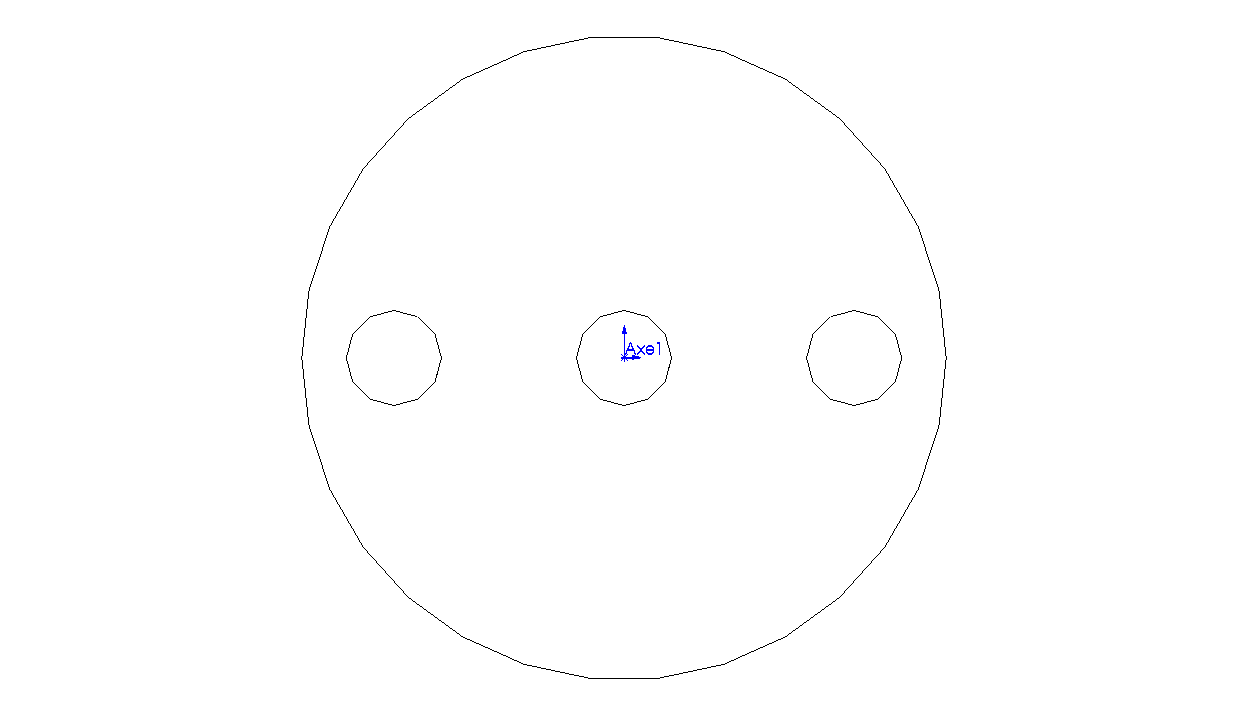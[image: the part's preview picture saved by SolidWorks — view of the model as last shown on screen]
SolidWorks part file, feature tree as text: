
SOLIDWORKS PART (.sldprt)
format: sldprt  version: not decoded by parser v0  size: 118,784 bytes
history: native  units: mm
features: sketch x5, plane x3, cut_extrude x3, extrude x2, material x1 (+8 scaffold rows collapsed)
feature tree (22):
  scaffold x8  (default folders/planes/origin — collapsed)
  material  "Matériau <non spécifié>"
  plane  "Plan de face"
  plane  "Plan de dessus"
  plane  "Plan de droite"
  sketch  "Esquisse1"  dims[D1=~1.672614mm]
  extrude  "Extrusion1"  Depth=6mm
  sketch  "Esquisse2"  dims[D1=~6.715216mm]
  extrude  "Extrusion2"  Depth=2mm
  sketch  "Esquisse3"  dims[D1=~2.022579mm]
  cut_extrude  "Enlèv. mat.-Extru.1"  [1 undecoded]
  sketch  "Esquisse4"  dims[D1=~1.487754mm]
  cut_extrude  "Enlèv. mat.-Extru.2"  [1 undecoded]
  sketch  "Esquisse5"  dims[D1=~0.796977mm]
  cut_extrude  "Enlèv. mat.-Extru.3"  Depth=10mm
decode coverage: 8 of 10 modeling features carry decoded parameters
note: ~ marks probable driven/reference dimensions
note: 2 parameter values undecoded
note: suppression state not decoded; provenance and decode notes live in map.json
